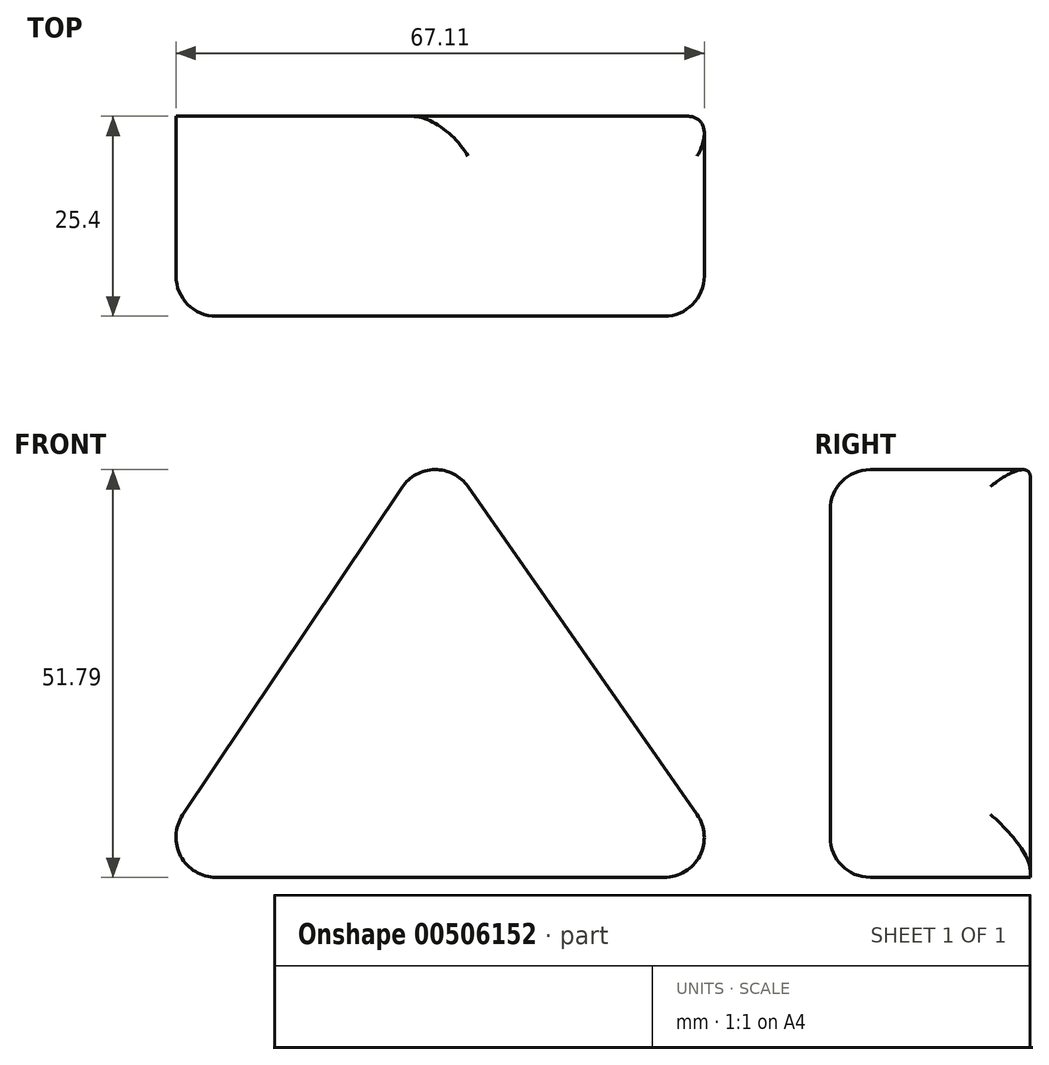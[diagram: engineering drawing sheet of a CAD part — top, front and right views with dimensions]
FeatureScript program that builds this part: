
annotation { "Feature Type Name" : "Feature", "Feature Type Description" : "" }
export const myFeature = defineFeature(function(context is Context, id is Id, definition is map)
    precondition{}
    {
        {
            var Q0;
            Q0=qCreatedBy(makeId("Front.planeOp"),FACE);
            var sketch = newSketch(context, id + "F0", { "sketchPlane" : qUnion([Q0])});
            skLineSegment(sketch, "E0", {"start": v(-37.27, 0) * mm, "end": v(38.93, 0) * mm});
            skLineSegment(sketch, "E1", {"start": v(-37.27, 0) * mm, "end": v(0, 55.71) * mm});
            skLineSegment(sketch, "E2", {"start": v(0, 55.71) * mm, "end": v(38.93, 0) * mm});
            skSolve(sketch);
        }
        {
            var Q0;
            Q0=makeQuery(id+"F0.imprint","IMPRINT",FACE,{"disambiguationData":[TD([[makeQuery(id+"F0.imprint","IMPRINT",EDGE,{"derivedFrom":sQuery(id+"F0.wireOp",EDGE,"E0")}),1.0]])]});
            extrude(context, id + "F1", {"entities" : qUnion([Q0]), "depth" : 25.4 * mm});
        }
        {
            var Q0;
            Q0=makeQuery(id+"F1.opExtrude","CAP_EDGE",EDGE,{"disambiguationData":[OSD([sQuery(id+"F0.wireOp",EDGE,"E1")])],"isStart":false});
            var Q1;
            Q1=makeQuery(id+"F1.opExtrude","CAP_EDGE",EDGE,{"disambiguationData":[OSD([sQuery(id+"F0.wireOp",EDGE,"E2")])],"isStart":false});
            var Q2;
            Q2=makeQuery(id+"F1.opExtrude","CAP_EDGE",EDGE,{"disambiguationData":[OSD([sQuery(id+"F0.wireOp",EDGE,"E0")])],"isStart":false});
            var Q3;
            Q3=makeQuery(id+"F1.opExtrude","SWEPT_EDGE",EDGE,{"disambiguationData":[OSD([sQuery(id+"F0.wireOp",EDGE,"E0"),sQuery(id+"F0.wireOp",EDGE,"E2")])]});
            var Q4;
            Q4=makeQuery(id+"F1.opExtrude","CAP_EDGE",EDGE,{"disambiguationData":[OSD([sQuery(id+"F0.wireOp",EDGE,"E2")])],"isStart":true});
            var Q5;
            Q5=makeQuery(id+"F1.opExtrude","SWEPT_EDGE",EDGE,{"disambiguationData":[OSD([sQuery(id+"F0.wireOp",EDGE,"E1"),sQuery(id+"F0.wireOp",EDGE,"E2")])]});
            var Q6;
            Q6=makeQuery(id+"F1.opExtrude","SWEPT_EDGE",EDGE,{"disambiguationData":[OSD([sQuery(id+"F0.wireOp",EDGE,"E0"),sQuery(id+"F0.wireOp",EDGE,"E1")])]});
            fillet(context, id + "F2", {"entities" : qUnion([Q0, Q1, Q2, Q3, Q4, Q5, Q6]), "radius" : 5.08 * mm, "tangentPropagation" : true, "allowEdgeOverflow" : false});
        }
    });
